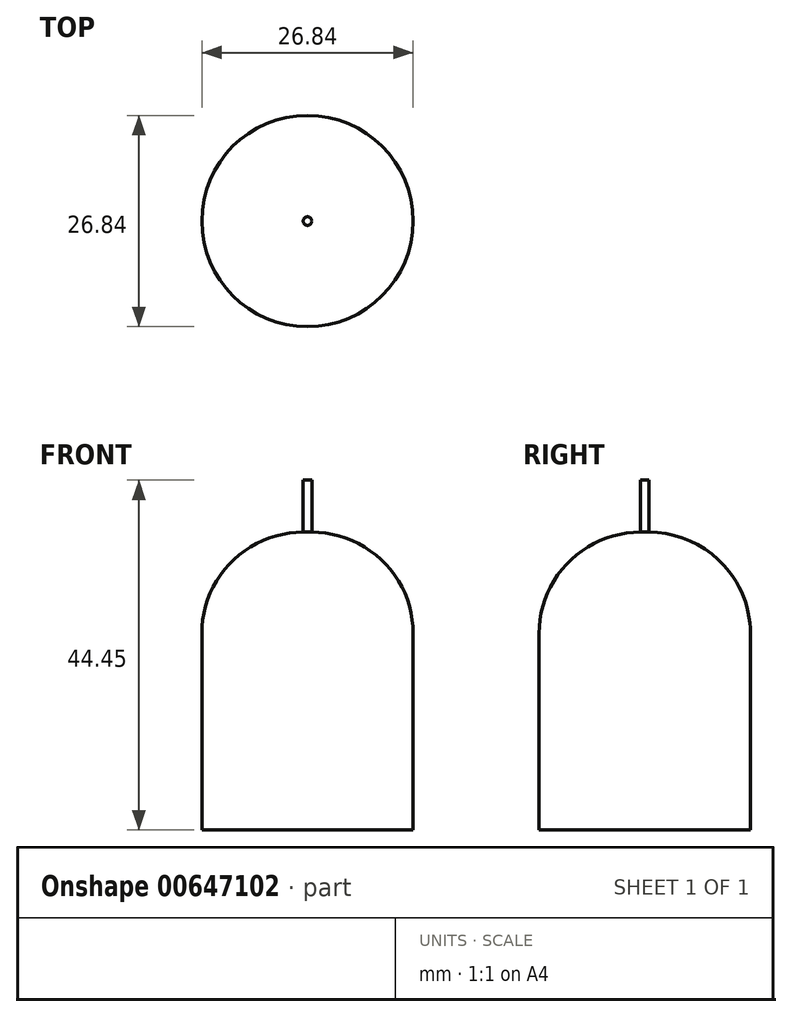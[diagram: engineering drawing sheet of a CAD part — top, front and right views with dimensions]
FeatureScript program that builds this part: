
annotation { "Feature Type Name" : "Feature", "Feature Type Description" : "" }
export const myFeature = defineFeature(function(context is Context, id is Id, definition is map)
    precondition{}
    {
        {
            var Q0;
            Q0=qCreatedBy(makeId("Top.planeOp"),FACE);
            var sketch = newSketch(context, id + "F0", { "sketchPlane" : qUnion([Q0])});
            skCircle(sketch, "E0", {"center": v(0, 0) * mm, "radius": 13.42 * mm});
            skSolve(sketch);
        }
        {
            var Q0;
            Q0 = qSketchRegion(id + "F0", true);
            var Q1;
            Q1=makeQuery(id+"F0.imprint","IMPRINT",FACE,{"disambiguationData":[TD([[makeQuery(id+"F0.imprint","IMPRINT",EDGE,{"derivedFrom":sQuery(id+"F0.wireOp",EDGE,"E0")}),1.0]])]});
            extrude(context, id + "F1", {"entities" : qUnion([Q0, Q1]), "depth" : 37.85 * mm, "offsetDistance" : 25.4 * mm});
        }
        {
            var Q0;
            Q0=makeQuery(id+"F1.opExtrude","CAP_EDGE",EDGE,{"disambiguationData":[OSD([sQuery(id+"F0.wireOp",EDGE,"E0")])],"isStart":false});
            fillet(context, id + "F2", {"entities" : qUnion([Q0]), "radius" : 12.88 * mm, "tangentPropagation" : true, "allowEdgeOverflow" : false});
        }
        {
            var Q0;
            Q0=makeQuery(id+"F1.opExtrude","CAP_FACE",FACE,{"disambiguationData":[OSD([sQuery(id+"F0.wireOp",EDGE,"E0")])],"isStart":false});
            extrude(context, id + "F3", {"entities" : qUnion([Q0]), "operationType" : NewBodyOperationType.ADD, "depth" : 6.6 * mm, "offsetDistance" : 25.4 * mm});
        }
    });
